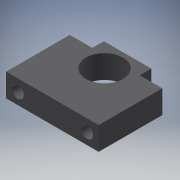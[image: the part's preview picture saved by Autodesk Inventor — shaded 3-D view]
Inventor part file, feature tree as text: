
AUTODESK INVENTOR PART (.ipt)
format: ipt  version: 2018 (Build 220112000, 112)  size: 144,896 bytes
history: native  units: mm
features: other x14, sketch x3, extrude x2, hole x1
ambient origin geometry x8: Origin, YZ Plane, XZ Plane, XY Plane, X Axis, Y Axis, Z Axis, Center Point
bodies: Solid1 (feature_tree)
feature tree (20):
  extrude  "Extrusion1"  Depth=55.0mm
  other  "bf_1_XY"
  other  "bf_1_YZ"
  other  "bf_1_ZX"
  other  "bf_1_X"
  other  "bf_1_Y"
  other  "bf_1_Z"
  other  "bf_1_Center"
  other  "bf_2x_XY"
  other  "bf_2x_YZ"
  other  "bf_2x_ZX"
  other  "bf_2x_X"
  other  "bf_2x_Y"
  other  "bf_2x_Z"
  other  "bf_2x_Center"
  hole  "Hole4"  [1 undecoded]
  extrude  "Extrusion2"  Depth=10.0mm
  sketch  "Sketch_1"  dims[d0=20.0mm d1=0.0mm d24=55.0mm]
  sketch  "Sketch6"  dims[d25=19.5mm d26=10.0mm]
  sketch  "Sketch7"  dims[d27=41.0mm d28=10.0mm d29=19.5mm d30=55.0mm d31=20.0mm d32=10.0mm d33=10.5mm d34=6.0mm d35=17.0mm d36=12.0mm d37=90.0deg d38=8.0mm d39=0.0mm d40=10.0mm d42=32.0mm d43=10.0mm d44=0.0mm]
note: 1 required parameter value undecoded (feature->parameter linkage not recoverable at this tier; creation-order binding heuristic only, values carry confidence <= 0.55)
